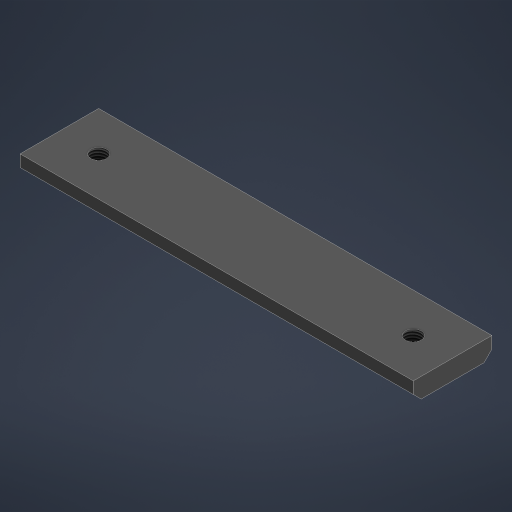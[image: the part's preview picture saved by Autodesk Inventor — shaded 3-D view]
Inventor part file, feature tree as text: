
AUTODESK INVENTOR PART (.ipt)
format: ipt  version: 2023 (Build 270158000, 158)  size: 184,320 bytes
history: native  units: mm
features: sketch x2, hole x2, thread x2, extrude x1, chamfer x1
ambient origin geometry x8: Origin, YZ Plane, XZ Plane, XY Plane, X Axis, Y Axis, Z Axis, Center Point
bodies: Solid1 (feature_tree)
feature tree (8):
  extrude  "Extrusion1"  Depth=20.0mm
  sketch  "Sketch2"  dims[d2=5.0mm d3=0.0mm d4=10.0mm d5=10.0mm d6=4.0mm d7=6.0mm d8=4.0mm d9=2.0mm d10=90.0deg d11=6.0mm d12=0.0mm d13=4.0mm d14=6.0mm d15=4.0mm d16=2.0mm d17=90.0deg d18=6.0mm d19=0.0mm d20=2.0mm d21=2.0mm d22=45.0deg d23=5.0mm d24=0.0mm d25=5.0mm d26=0.0mm]
  hole  "Hole1"  [1 undecoded]
  hole  "Hole2"  [1 undecoded]
  chamfer  "Chamfer1"  Distance=2.0mm Angle=45.0deg
  thread  "Thread1"  [1 undecoded]
  thread  "Thread2"  [1 undecoded]
  sketch  "Sketch1"  dims[d0=100.0mm d1=20.0mm]
note: 4 required parameter values undecoded (feature->parameter linkage not recoverable at this tier; creation-order binding heuristic only, values carry confidence <= 0.55)
